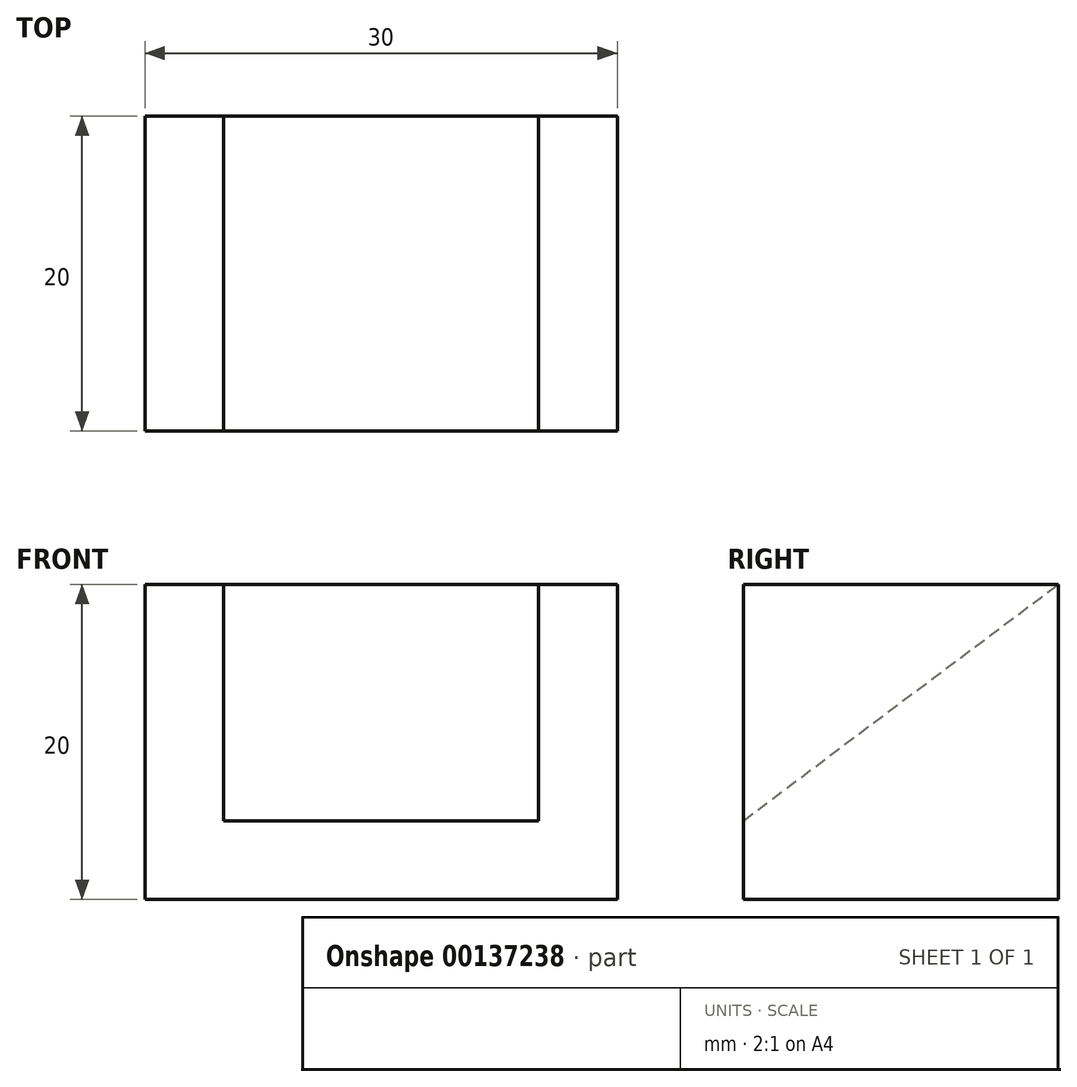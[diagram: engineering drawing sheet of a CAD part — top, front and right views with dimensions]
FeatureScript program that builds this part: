
annotation { "Feature Type Name" : "Feature", "Feature Type Description" : "" }
export const myFeature = defineFeature(function(context is Context, id is Id, definition is map)
    precondition{}
    {
        {
            var Q0;
            Q0=qCreatedBy(makeId("Right.planeOp"),FACE);
            var sketch = newSketch(context, id + "F0", { "sketchPlane" : qUnion([Q0])});
            skLineSegment(sketch, "E0.bottom", {"start": v(0, 0) * mm, "end": v(-20, 0) * mm});
            skLineSegment(sketch, "E0.top", {"start": v(0, 20) * mm, "end": v(-20, 20) * mm});
            skLineSegment(sketch, "E0.left", {"start": v(0, 0) * mm, "end": v(0, 20) * mm});
            skLineSegment(sketch, "E0.right", {"start": v(-20, 0) * mm, "end": v(-20, 20) * mm});
            skSolve(sketch);
        }
        {
            var Q0;
            Q0 = qSketchRegion(id + "F0", true);
            extrude(context, id + "F1", {"entities" : qUnion([Q0]), "endBound" : BoundingType.SYMMETRIC, "depth" : 30 * mm});
        }
        {
            var Q0;
            Q0=qCreatedBy(makeId("Right.planeOp"),FACE);
            var sketch = newSketch(context, id + "F2", { "sketchPlane" : qUnion([Q0])});
            skLineSegment(sketch, "E1", {"start": v(0, 20) * mm, "end": v(-20, 20) * mm});
            skLineSegment(sketch, "E2", {"start": v(-20, 20) * mm, "end": v(-20, 5) * mm});
            skLineSegment(sketch, "E3", {"start": v(-20, 5) * mm, "end": v(0, 20) * mm});
            skSolve(sketch);
        }
        {
            var Q0;
            Q0 = qSketchRegion(id + "F2", true);
            extrude(context, id + "F3", {"entities" : qUnion([Q0]), "operationType" : NewBodyOperationType.REMOVE, "endBound" : BoundingType.SYMMETRIC, "depth" : 20 * mm});
        }
    });
